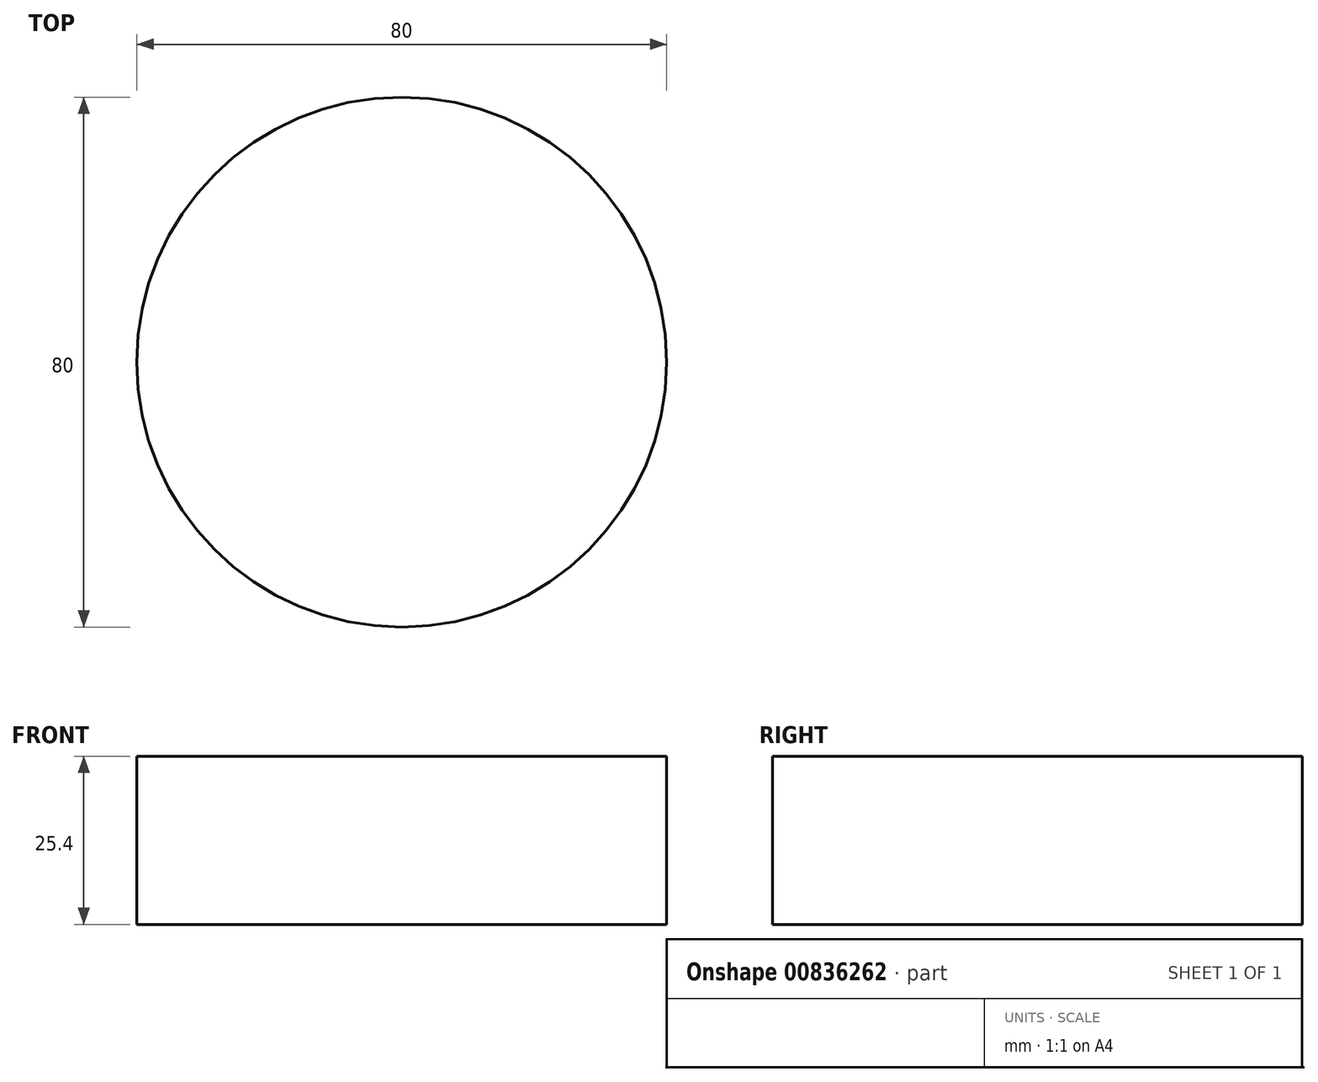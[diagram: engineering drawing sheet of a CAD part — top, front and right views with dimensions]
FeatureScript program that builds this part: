
annotation { "Feature Type Name" : "Feature", "Feature Type Description" : "" }
export const myFeature = defineFeature(function(context is Context, id is Id, definition is map)
    precondition{}
    {
        {
            var Q0;
            Q0=qCreatedBy(makeId("Top.planeOp"),FACE);
            var sketch = newSketch(context, id + "F0", { "sketchPlane" : qUnion([Q0])});
            skCircle(sketch, "E0", {"center": v(0, 0) * mm, "radius": 40 * mm});
            skSolve(sketch);
        }
        {
            var Q0;
            Q0=sQuery(id+"F0.wireOp",EDGE,"E0");
            extrude(context, id + "F1", {"bodyType" : ToolBodyType.SURFACE, "surfaceEntities" : qUnion([Q0]), "depth" : 25.4 * mm, "offsetDistance" : 25.4 * mm});
        }
    });
